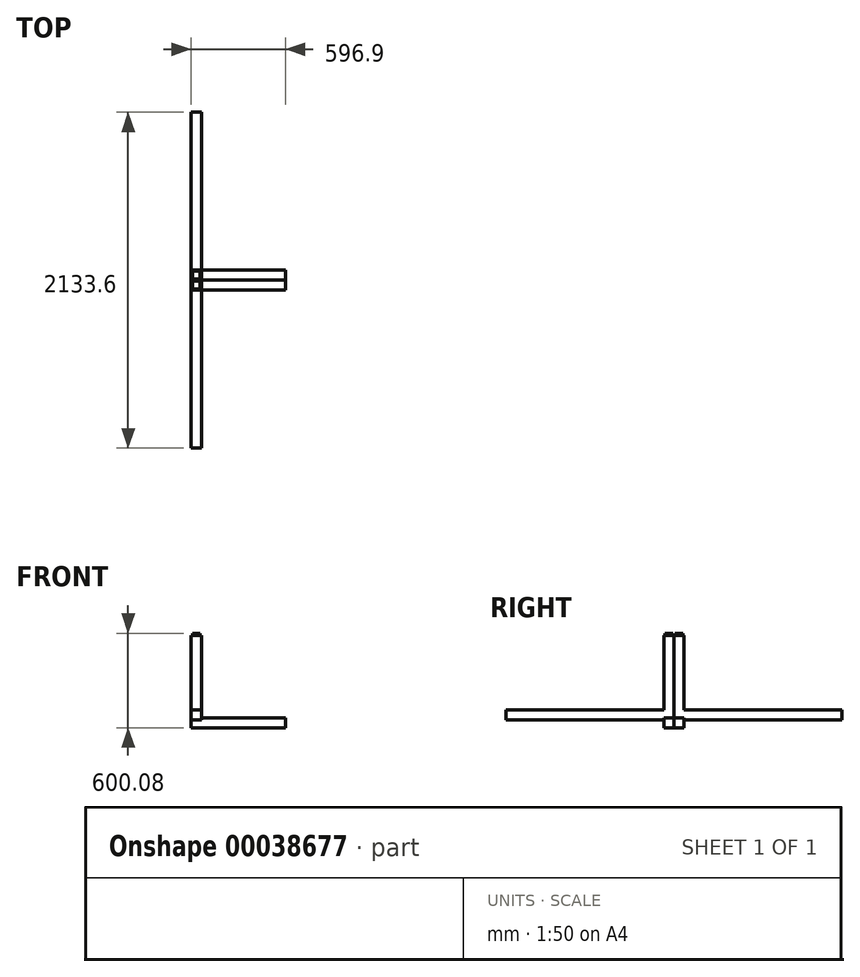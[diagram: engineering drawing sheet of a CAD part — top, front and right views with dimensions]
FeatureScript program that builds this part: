
annotation { "Feature Type Name" : "Feature", "Feature Type Description" : "" }
export const myFeature = defineFeature(function(context is Context, id is Id, definition is map)
    precondition{}
    {
        {
            var Q0;
            Q0=qCreatedBy(makeId("Top.planeOp"),FACE);
            var sketch = newSketch(context, id + "F0", { "sketchPlane" : qUnion([Q0])});
            skLineSegment(sketch, "E0.bottom", {"start": v(0, 0) * mm, "end": v(63.5, 0) * mm});
            skLineSegment(sketch, "E0.top", {"start": v(0, -63.5) * mm, "end": v(63.5, -63.5) * mm});
            skLineSegment(sketch, "E0.left", {"start": v(0, 0) * mm, "end": v(0, -63.5) * mm});
            skLineSegment(sketch, "E0.right", {"start": v(63.5, 0) * mm, "end": v(63.5, -63.5) * mm});
            skSolve(sketch);
        }
        {
            var Q0;
            Q0=makeQuery(id+"F0.imprint","IMPRINT",FACE,{"disambiguationData":[TD([[makeQuery(id+"F0.imprint","IMPRINT",EDGE,{"derivedFrom":sQuery(id+"F0.wireOp",EDGE,"E0.bottom")}),-1.0]])]});
            extrude(context, id + "F1", {"entities" : qUnion([Q0]), "depth" : 600.07 * mm});
        }
        {
            var Q0;
            Q0=makeQuery(id+"F1.opExtrude","CAP_FACE",FACE,{"disambiguationData":[OSD([sQuery(id+"F0.wireOp",EDGE,"E0.bottom"),sQuery(id+"F0.wireOp",EDGE,"E0.top"),sQuery(id+"F0.wireOp",EDGE,"E0.left"),sQuery(id+"F0.wireOp",EDGE,"E0.right")])],"isStart":false});
            var sketch = newSketch(context, id + "F2", { "sketchPlane" : qUnion([Q0])});
            skLineSegment(sketch, "E1.0", {"start": v(6.35, -57.15) * mm, "end": v(57.15, -57.15) * mm});
            skLineSegment(sketch, "E1.1", {"start": v(6.35, -6.35) * mm, "end": v(6.35, -57.15) * mm});
            skLineSegment(sketch, "E1.2", {"start": v(6.35, -6.35) * mm, "end": v(57.15, -6.35) * mm});
            skLineSegment(sketch, "E1.3", {"start": v(57.15, -6.35) * mm, "end": v(57.15, -57.15) * mm});
            skSolve(sketch);
        }
        {
            var Q0;
            Q0=makeQuery(id+"F2.imprint","IMPRINT",FACE,{"disambiguationData":[TD([[makeQuery(id+"F2.imprint","IMPRINT",EDGE,{"derivedFrom":sQuery(id+"F2.wireOp",EDGE,"E1.0")}),-1.0]])]});
            extrude(context, id + "F3", {"entities" : qUnion([Q0]), "operationType" : NewBodyOperationType.REMOVE, "oppositeDirection" : true, "depth" : 12.7 * mm});
        }
        {
            var Q0;
            Q0=makeQuery(id+"F1.opExtrude","SWEPT_FACE",FACE,{"disambiguationData":[OSD([sQuery(id+"F0.wireOp",EDGE,"E0.top")])]});
            var sketch = newSketch(context, id + "F4", { "sketchPlane" : qUnion([Q0])});
            skLineSegment(sketch, "E2.bottom", {"start": v(0, 114.3) * mm, "end": v(63.5, 114.3) * mm});
            skLineSegment(sketch, "E2.top", {"start": v(0, 50.8) * mm, "end": v(63.5, 50.8) * mm});
            skLineSegment(sketch, "E2.left", {"start": v(0, 114.3) * mm, "end": v(0, 50.8) * mm});
            skLineSegment(sketch, "E2.right", {"start": v(63.5, 114.3) * mm, "end": v(63.5, 50.8) * mm});
            skSolve(sketch);
        }
        {
            var Q0;
            {var subQ0=sQuery(id+"F4.wireOp",EDGE,"E2.right");Q0=makeQuery(id+"F4.imprint","IMPRINT",FACE,{"disambiguationData":[TD([[makeQuery(id+"F4.imprint","IMPRINT",EDGE,{"derivedFrom":subQ0}),-1.0]])]});}
            var Q1;
            {var subQ0=sQuery(id+"F4.wireOp",EDGE,"E2.left");Q1=makeQuery(id+"F4.imprint","IMPRINT",FACE,{"disambiguationData":[TD([[makeQuery(id+"F4.imprint","IMPRINT",EDGE,{"derivedFrom":subQ0}),1.0]])]});}
            extrude(context, id + "F5", {"entities" : qUnion([Q0, Q1]), "depth" : 501.65 * mm});
        }
        {
            var Q0;
            Q0=makeQuery(id+"F5.opExtrude","SWEPT_BODY",BODY,{"disambiguationData":[OSD([sQuery(id+"F4.wireOp",EDGE,"E2.bottom"),sQuery(id+"F4.wireOp",EDGE,"E2.top"),sQuery(id+"F4.wireOp",EDGE,"E2.left"),sQuery(id+"F4.wireOp",EDGE,"E2.right")])]});
            var Q1;
            Q1=makeQuery(id+"F5.opExtrude","CAP_FACE",FACE,{"disambiguationData":[OSD([sQuery(id+"F4.wireOp",EDGE,"E2.bottom"),sQuery(id+"F4.wireOp",EDGE,"E2.top"),sQuery(id+"F4.wireOp",EDGE,"E2.left"),sQuery(id+"F4.wireOp",EDGE,"E2.right")])],"isStart":false});
            mirror(context, id + "F6", {"operationType" : NewBodyOperationType.ADD, "entities" : qUnion([Q0]), "mirrorPlane" : qUnion([Q1])});
        }
        {
            var Q0;
            Q0=qCreatedBy(makeId("Right.planeOp"),FACE);
            var sketch = newSketch(context, id + "F7", { "sketchPlane" : qUnion([Q0])});
            skLineSegment(sketch, "E3.bottom", {"start": v(0, 63.5) * mm, "end": v(-63.5, 63.5) * mm});
            skLineSegment(sketch, "E3.top", {"start": v(0, 0) * mm, "end": v(-63.5, 0) * mm});
            skLineSegment(sketch, "E3.left", {"start": v(0, 63.5) * mm, "end": v(0, 0) * mm});
            skLineSegment(sketch, "E3.right", {"start": v(-63.5, 63.5) * mm, "end": v(-63.5, 0) * mm});
            skSolve(sketch);
        }
        {
            var Q0;
            Q0 = qSketchRegion(id + "F7", true);
            extrude(context, id + "F8", {"entities" : qUnion([Q0]), "depth" : 298.45 * mm});
        }
        {
            var Q0;
            Q0=makeQuery(id+"F8.opExtrude","SWEPT_BODY",BODY,{"disambiguationData":[OSD([sQuery(id+"F7.wireOp",EDGE,"E3.bottom"),sQuery(id+"F7.wireOp",EDGE,"E3.top"),sQuery(id+"F7.wireOp",EDGE,"E3.left"),sQuery(id+"F7.wireOp",EDGE,"E3.right")])]});
            var Q1;
            Q1=makeQuery(id+"F8.opExtrude","CAP_FACE",FACE,{"disambiguationData":[OSD([sQuery(id+"F7.wireOp",EDGE,"E3.bottom"),sQuery(id+"F7.wireOp",EDGE,"E3.top"),sQuery(id+"F7.wireOp",EDGE,"E3.left"),sQuery(id+"F7.wireOp",EDGE,"E3.right")])],"isStart":false});
            mirror(context, id + "F9", {"operationType" : NewBodyOperationType.ADD, "entities" : qUnion([Q0]), "mirrorPlane" : qUnion([Q1])});
        }
        {
            var Q0;
            Q0=makeQuery(id+"F1.opExtrude","SWEPT_BODY",BODY,{"disambiguationData":[OSD([sQuery(id+"F0.wireOp",EDGE,"E0.bottom"),sQuery(id+"F0.wireOp",EDGE,"E0.top"),sQuery(id+"F0.wireOp",EDGE,"E0.left"),sQuery(id+"F0.wireOp",EDGE,"E0.right")])]});
            var Q1;
            Q1=qCreatedBy(makeId("Front.planeOp"),FACE);
            mirror(context, id + "F10", {"entities" : qUnion([Q0]), "mirrorPlane" : qUnion([Q1])});
        }
    });
